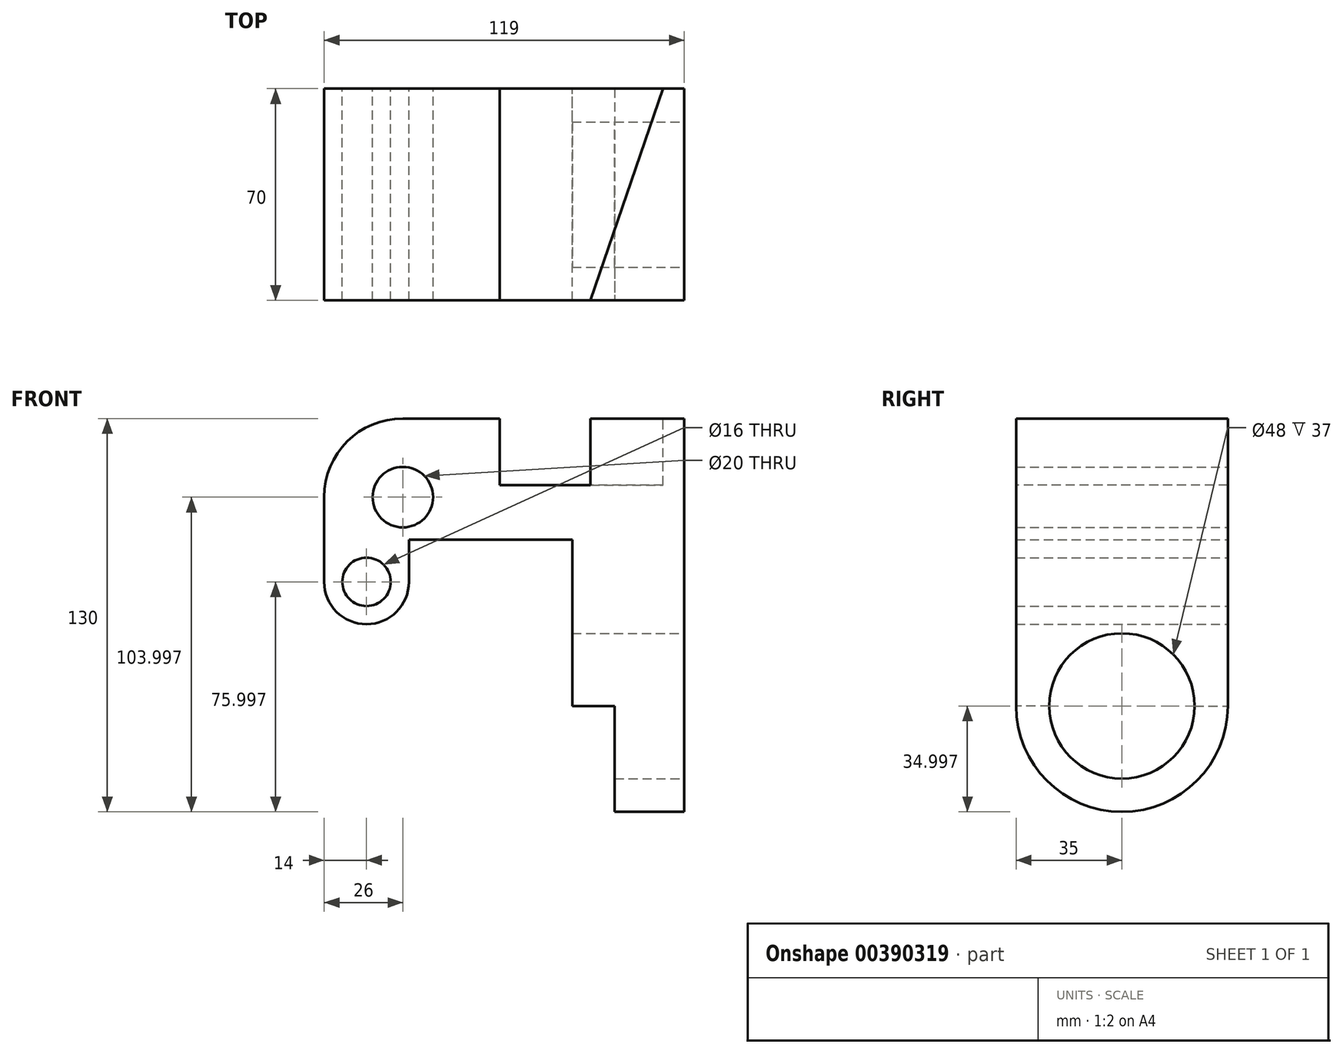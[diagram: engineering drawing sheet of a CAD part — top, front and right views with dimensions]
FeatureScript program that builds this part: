
annotation { "Feature Type Name" : "Feature", "Feature Type Description" : "" }
export const myFeature = defineFeature(function(context is Context, id is Id, definition is map)
    precondition{}
    {
        {
            var Q0;
            Q0=qCreatedBy(makeId("Front.planeOp"),FACE);
            var sketch = newSketch(context, id + "F0", { "sketchPlane" : qUnion([Q0])});
            skLineSegment(sketch, "E0.top", {"start": v(65, -15.1) * mm, "end": v(-54, -15.1) * mm});
            skPoint(sketch, "E0.middle", {"position": v(0, 0) * mm});
            skLineSegment(sketch, "E1.bottom", {"start": v(65, -15.1) * mm, "end": v(28, -15.1) * mm});
            skLineSegment(sketch, "E1.top", {"start": v(65, -70.1) * mm, "end": v(28, -70.1) * mm});
            skLineSegment(sketch, "E1.left", {"start": v(65, -15.1) * mm, "end": v(65, -70.1) * mm});
            skLineSegment(sketch, "E1.right", {"start": v(28, -15.1) * mm, "end": v(28, -70.1) * mm});
            skLineSegment(sketch, "E2.bottom", {"start": v(-54, -15.1) * mm, "end": v(-26, -15.1) * mm});
            skLineSegment(sketch, "E2.top", {"start": v(-54, -29.1) * mm, "end": v(-26, -29.1) * mm});
            skLineSegment(sketch, "E2.left", {"start": v(-54, -15.1) * mm, "end": v(-54, -29.1) * mm});
            skLineSegment(sketch, "E2.right", {"start": v(-26, -15.1) * mm, "end": v(-26, -29.1) * mm});
            skArc(sketch, "E3", {"start": v(-54, -29.1) * mm, "mid": v(-40, -43.1) * mm, "end": v(-26, -29.1) * mm});
            skLineSegment(sketch, "E4", {"start": v(65, -15.1) * mm, "end": v(65, 24.9) * mm});
            skLineSegment(sketch, "E5", {"start": v(65, 24.9) * mm, "end": v(-28, 24.9) * mm});
            skArc(sketch, "E6", {"start": v(-28, 24.9) * mm, "mid": v(-46.38, 17.28) * mm, "end": v(-54, -1.1) * mm});
            skLineSegment(sketch, "E7", {"start": v(-54, -1.1) * mm, "end": v(-54, -15.1) * mm});
            skCircle(sketch, "E8", {"center": v(-40, -29.1) * mm, "radius": 8 * mm});
            skCircle(sketch, "E9", {"center": v(-28, -1.1) * mm, "radius": 10 * mm});
            skSolve(sketch);
        }
        {
            var Q0;
            Q0 = qSketchRegion(id + "F0", true);
            extrude(context, id + "F1", {"entities" : qUnion([Q0]), "endBound" : BoundingType.SYMMETRIC, "depth" : 70 * mm});
        }
        {
            var Q0;
            Q0=makeQuery(id+"F1.opExtrude","SWEPT_FACE",FACE,{"disambiguationData":[OSD([sQuery(id+"F0.wireOp",EDGE,"E5")])]});
            var sketch = newSketch(context, id + "F2", { "sketchPlane" : qUnion([Q0])});
            skLineSegment(sketch, "E10", {"start": v(4, 35) * mm, "end": v(4, -35) * mm});
            skLineSegment(sketch, "E11", {"start": v(4, -35) * mm, "end": v(34, -35) * mm});
            skLineSegment(sketch, "E12", {"start": v(34, -35) * mm, "end": v(58, 35) * mm});
            skLineSegment(sketch, "E13", {"start": v(58, 35) * mm, "end": v(4, 35) * mm});
            skSolve(sketch);
        }
        {
            var Q0;
            Q0 = qSketchRegion(id + "F2", true);
            extrude(context, id + "F3", {"entities" : qUnion([Q0]), "operationType" : NewBodyOperationType.REMOVE, "oppositeDirection" : true, "depth" : 22 * mm});
        }
        {
            var Q0;
            Q0=makeQuery(id+"F1.opExtrude","SWEPT_FACE",FACE,{"disambiguationData":[OSD([sQuery(id+"F0.wireOp",EDGE,"E1.top")])]});
            var sketch = newSketch(context, id + "F4", { "sketchPlane" : qUnion([Q0])});
            skLineSegment(sketch, "E14.bottom", {"start": v(42, 35) * mm, "end": v(65, 35) * mm});
            skLineSegment(sketch, "E14.top", {"start": v(42, 0) * mm, "end": v(65, 0) * mm});
            skLineSegment(sketch, "E14.left", {"start": v(42, 35) * mm, "end": v(42, 0) * mm});
            skLineSegment(sketch, "E14.right", {"start": v(65, 35) * mm, "end": v(65, 0) * mm});
            skSolve(sketch);
        }
        {
            var Q0;
            Q0=makeQuery(id+"F4.imprint","IMPRINT",FACE,{"disambiguationData":[TD([[makeQuery(id+"F4.imprint","IMPRINT",EDGE,{"derivedFrom":sQuery(id+"F4.wireOp",EDGE,"E14.bottom")}),1.0]])]});
            var Q1;
            Q1=sQuery(id+"F4.wireOp",EDGE,"E14.top");
            revolve(context, id + "F5", {"operationType" : NewBodyOperationType.ADD, "entities" : qUnion([Q0]), "axis" : qUnion([Q1]), "revolveType" : RevolveType.FULL});
        }
        {
            var Q0;
            Q0=makeQuery(id+"F5.boolean.opBoolean","MERGE",FACE,{"derivedFrom":[makeQuery(id+"F1.opExtrude","SWEPT_FACE",FACE,{"disambiguationData":[OSD([sQuery(id+"F0.wireOp",EDGE,"E1.left"),sQuery(id+"F0.wireOp",EDGE,"E4")])]}),makeQuery(id+"F5.opRevolve","SWEPT_FACE",FACE,{"disambiguationData":[OSD([sQuery(id+"F4.wireOp",EDGE,"E14.right")])]})]});
            var sketch = newSketch(context, id + "F6", { "sketchPlane" : qUnion([Q0])});
            skCircle(sketch, "E15", {"center": v(0, -70.1) * mm, "radius": 24 * mm});
            skSolve(sketch);
        }
        {
            var Q0;
            Q0 = qSketchRegion(id + "F6", true);
            extrude(context, id + "F7", {"entities" : qUnion([Q0]), "operationType" : NewBodyOperationType.REMOVE, "oppositeDirection" : true, "depth" : 37 * mm});
        }
    });
